annotation { "Feature Type Name" : "Feature", "Feature Type Description" : "" }
export const myFeature = defineFeature(function(context is Context, id is Id, definition is map)
    precondition{}
    {
        {
            var Q0;
            Q0=qCreatedBy(makeId("Front.planeOp"),FACE);
            var sketch = newSketch(context, id + "F0", { "sketchPlane" : qUnion([Q0])});
            skLineSegment(sketch, "E0", {"start": v(-160.19, 53.69) * mm, "end": v(-160.19, -60.61) * mm, "construction": true});
            skLineSegment(sketch, "E1", {"start": v(-160.19, -60.61) * mm, "end": v(-115.74, -60.61) * mm, "construction": true});
            skCircle(sketch, "E2", {"center": v(-160.19, 53.69) * mm, "radius": 9.53 * mm});
            skCircle(sketch, "E3", {"center": v(-160.19, 2.89) * mm, "radius": 15.88 * mm});
            skCircle(sketch, "E4", {"center": v(-160.19, -60.61) * mm, "radius": 10.66 * mm});
            skCircle(sketch, "E5", {"center": v(-115.74, -60.61) * mm, "radius": 7.94 * mm});
            skCircle(sketch, "E6", {"center": v(-160.19, 53.69) * mm, "radius": 3.18 * mm});
            skLineSegment(sketch, "E7", {"start": v(-150.74, 54.88) * mm, "end": v(-144.44, 4.87) * mm});
            skLineSegment(sketch, "E8", {"start": v(-159.54, -71.25) * mm, "end": v(-115.25, -68.53) * mm});
            skLineSegment(sketch, "E9", {"start": v(-148, -42.55) * mm, "end": v(-144.37, 1.59) * mm});
            skLineSegment(sketch, "E10", {"start": v(-169.64, 54.88) * mm, "end": v(-175.94, 4.87) * mm});
            skLineSegment(sketch, "E11", {"start": v(-140.57, -51.14) * mm, "end": v(-115.25, -52.69) * mm});
            skLineSegment(sketch, "E12", {"start": v(-176, 1.59) * mm, "end": v(-170.8, -61.49) * mm});
            skCircle(sketch, "E13", {"center": v(-160.19, 2.89) * mm, "radius": 3.18 * mm});
            skCircle(sketch, "E14", {"center": v(-160.19, -60.61) * mm, "radius": 3.18 * mm});
            skCircle(sketch, "E15", {"center": v(-115.74, -60.61) * mm, "radius": 3.18 * mm});
            skCircle(sketch, "E16", {"center": v(-162.37, 39.41) * mm, "radius": 1.59 * mm});
            skArc(sketch, "E17.filletArc", {"start": v(-148, -42.55) * mm, "mid": v(-146.1, -48.4) * mm, "end": v(-140.57, -51.14) * mm});
            skText(sketch, "E18", { "text": "0.728 in3\n", "fontName": "OpenSans-Regular.ttf"});
            skText(sketch, "E19", { "text": "Jaheim Goffigon", "fontName": "OpenSans-Regular.ttf"});
            const initialGuessF0  = {"E18": [-0.0686, 0.0422, 1, 0, 0.01047], "E19": [-0.06493, 0.00966, 1, 0, 0.01011]};
            skSetInitialGuess(sketch, initialGuessF0);
            skSolve(sketch);
        }
        {
            var Q0;
            Q0 = qSketchRegion(id + "F0", true);
            extrude(context, id + "F1", {"entities" : qUnion([Q0]), "depth" : 3.05 * mm, "offsetDistance" : 25.4 * mm});
        }
    });